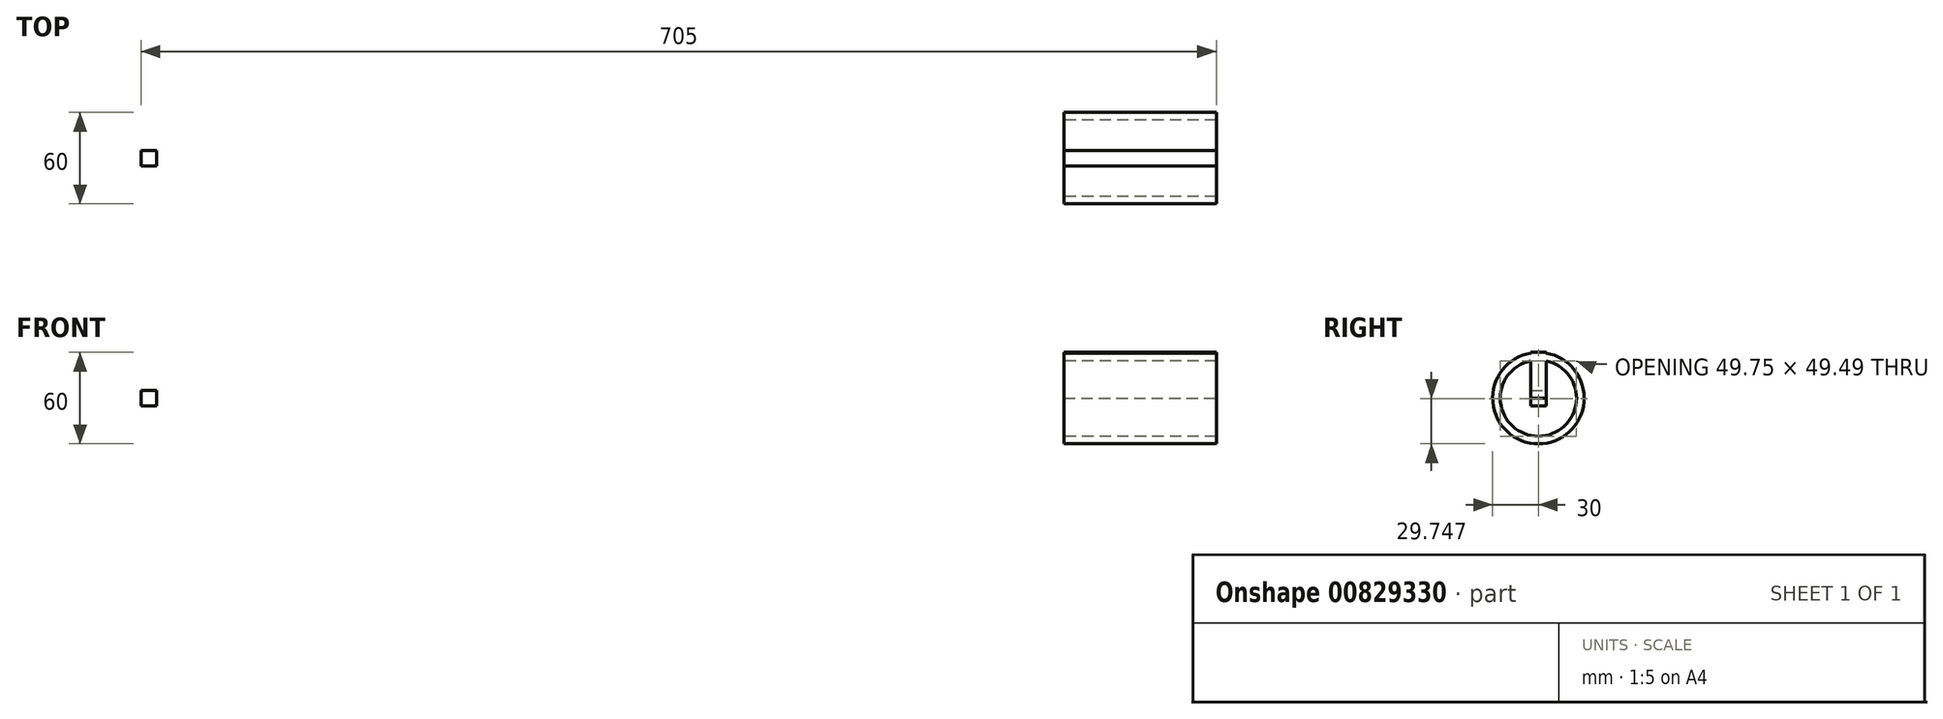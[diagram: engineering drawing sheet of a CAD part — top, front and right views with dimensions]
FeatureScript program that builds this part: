
annotation { "Feature Type Name" : "Feature", "Feature Type Description" : "" }
export const myFeature = defineFeature(function(context is Context, id is Id, definition is map)
    precondition{}
    {
        {
            var Q0;
            Q0=qCreatedBy(makeId("Front.planeOp"),FACE);
            var sketch = newSketch(context, id + "F0", { "sketchPlane" : qUnion([Q0])});
            skLineSegment(sketch, "E0", {"start": v(0, 0) * mm, "end": v(600, 0) * mm});
            skLineSegment(sketch, "E1.bottom", {"start": v(600, 0) * mm, "end": v(700, 0) * mm});
            skLineSegment(sketch, "E1.top", {"start": v(600, 30) * mm, "end": v(700, 30) * mm});
            skLineSegment(sketch, "E1.left", {"start": v(600, 0) * mm, "end": v(600, 30) * mm});
            skLineSegment(sketch, "E1.right", {"start": v(700, 0) * mm, "end": v(700, 30) * mm});
            skLineSegment(sketch, "E2.0", {"start": v(600, 25) * mm, "end": v(700, 25) * mm});
            skLineSegment(sketch, "E3.bottom", {"start": v(5, -5) * mm, "end": v(-5, -5) * mm});
            skLineSegment(sketch, "E3.top", {"start": v(5, 5) * mm, "end": v(-5, 5) * mm});
            skLineSegment(sketch, "E3.left", {"start": v(5, -5) * mm, "end": v(5, 5) * mm});
            skLineSegment(sketch, "E3.right", {"start": v(-5, -5) * mm, "end": v(-5, 5) * mm});
            skPoint(sketch, "E3.middle", {"position": v(0, 0) * mm});
            skSolve(sketch);
        }
        {
            var Q0;
            {var subQ0=sQuery(id+"F0.wireOp",EDGE,"E1.top");Q0=makeQuery(id+"F0.imprint","IMPRINT",FACE,{"disambiguationData":[TD([[makeQuery(id+"F0.imprint","IMPRINT",EDGE,{"derivedFrom":subQ0}),-1.0]])]});}
            var Q1;
            Q1=sQuery(id+"F0.wireOp",EDGE,"E1.bottom");
            revolve(context, id + "F1", {"surfaceOperationType" : NewSurfaceOperationType.NEW, "entities" : qUnion([Q0]), "axis" : qUnion([Q1]), "revolveType" : RevolveType.FULL});
        }
        {
            var Q0;
            Q0=qSketchRegion(id+"F0",true);
            extrude(context, id + "F2", {"entities" : qUnion([Q0]), "operationType" : NewBodyOperationType.ADD, "endBound" : BoundingType.SYMMETRIC, "depth" : 10 * mm, "offsetDistance" : 25 * mm});
        }
    });
